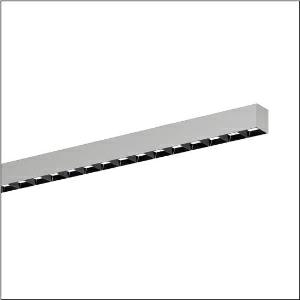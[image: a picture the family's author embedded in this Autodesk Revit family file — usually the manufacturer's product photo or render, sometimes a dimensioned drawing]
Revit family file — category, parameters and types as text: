
# Revit family: silica_r__21_51mx24dc4asb_83d0
name_source: partatom
category: Lighting Fixtures
units: mm (PartAtom-declared; Revit-internal decimal feet)

## family parameters
Cut with Voids When Loaded = No
Host = Face
Light Source = No
Part Type = Normal
Room Calculation Point = No
Round Connector Dimension = Use Diameter
Shared = No

## types (1)
- --- (1 x LED, 10800 lm, 73.7 W, 4000K)
    Apparent Load = 74 VA
    CIE Flux Codes = 74 94 99 100 100
    Color Rendering = 80
    Color Temperature = 4000K
    Default Elevation = 1800 mm
    Description = Silica® 21, office luminaire, primary light control with darklight reflector, of PMMA, black, CAT 2 (L<= 3000cd/m²), light emission: direct distribution, primary light characteristic: asymmetric, installation type: surface-mounted, LED, rated luminous flux: 10.800lm, luminous efficacy: 147lm/W, light colour: 840, colour temperature: 4000K, with terminal, 3+2-pole, max. 2.5mm², mains connection: 220..240V, AC, 50/60Hz, rated input power: 73.7W, luminaire housing, of aluminium, metallic grey (RAL 9006), length: 3.004mm, width: 53mm, height: 53mm, protection rating (complete): IP20, insulation class (complete): insulation class I (protective earthing), certification: CE, permissible operating ambient temperature: 0..+35°C, standard: EN 50419, packaging unit: 1 piece
    Height = 0 mm  [stored 0 ft]
    Lamp = 1 x LED
    Lamp Light Flux = 10800 lm
    Lamp Power = 73.7 W
    Lamp count = 1
    Length = 3004 mm
    Luminous efficacy = 147 lm/W
    Manufacturer = Siteco
    ModVariant = No
    Model = 51MX24DC4ASB
    Mounting Place = Ceiling
    Mounting Type = Recessed
    Number of Poles = 1
    OnlyDefault = Yes
    Power Factor = 1
    Product Name = Silica® 21
    Product group = office luminaire | ceiling recessed
    ProductGroupID = 401
    Protection Class = Protection class I
    Protection Degree = IP 20
    RLX_Detail_Level = 1
    RLX_Emergency_Light_Flux = 0 lm
    RLX_Emergency_Type = 0
    RLX_Emergency_Type_DB = No
    RlxData = <blob elided: 63733 chars, md5=dfa169b8>
    Socket = socket
    Standby Power = 0 W
    System Light Flux = 10800 lm
    System Power = 74 W
    Type Comments = factory setting: luminous flux: 100 % | dim-lin: 254 | 418 mA
    Type Image = l_1297764.jpg
    URL = http://relux.com
    VarID = @adj_053309
    Voltage = 0 V
    Weight = 0.00 kg
    Width = 53 mm

note: [stored X ft] marks values corroborated as IEEE doubles in the binary element streams (Revit-internal decimal feet)

## geometry (parser evidence)
native form markers: Blend x4, Sweep x10
no freeform markers — native parametric forms only
